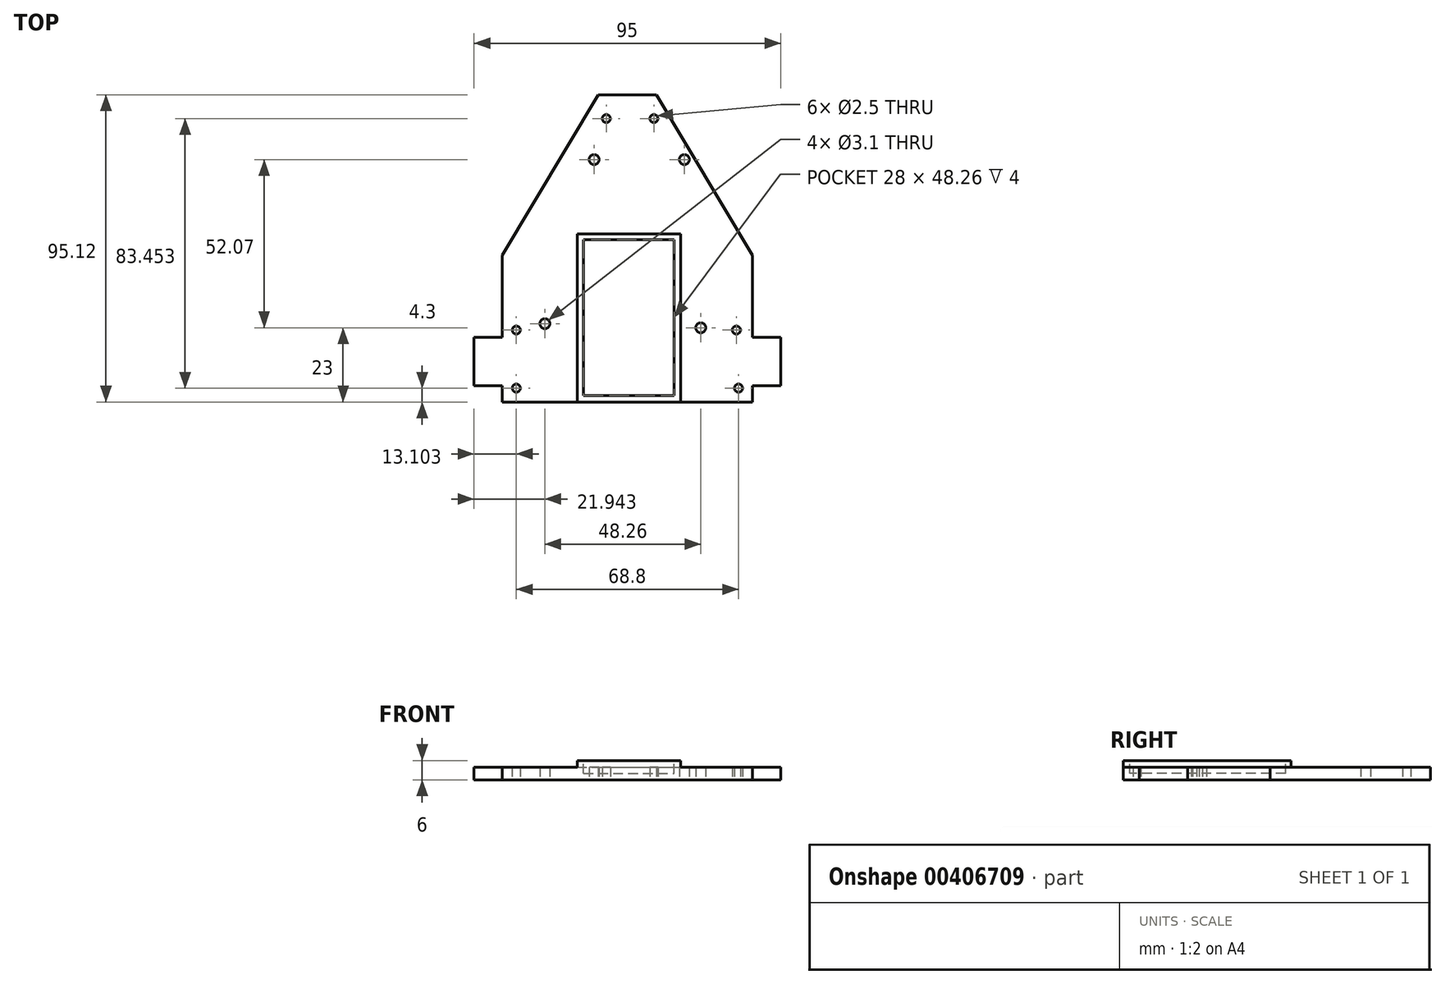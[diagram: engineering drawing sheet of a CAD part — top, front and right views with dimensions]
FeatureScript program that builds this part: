
annotation { "Feature Type Name" : "Feature", "Feature Type Description" : "" }
export const myFeature = defineFeature(function(context is Context, id is Id, definition is map)
    precondition{}
    {
        {
            var Q0;
            Q0=qCreatedBy(makeId("Top.planeOp"),FACE);
            var sketch = newSketch(context, id + "F0", { "sketchPlane" : qUnion([Q0])});
            skLineSegment(sketch, "E0", {"start": v(-31.63, 74.2) * mm, "end": v(-13.63, 74.2) * mm});
            skLineSegment(sketch, "E1", {"start": v(-13.63, 74.2) * mm, "end": v(16.07, 24.57) * mm});
            skLineSegment(sketch, "E2", {"start": v(16.07, 24.57) * mm, "end": v(16.07, -0.93) * mm});
            skLineSegment(sketch, "E3", {"start": v(16.07, -0.93) * mm, "end": v(24.87, -0.93) * mm});
            skLineSegment(sketch, "E4", {"start": v(24.87, -0.93) * mm, "end": v(24.87, -15.93) * mm});
            skLineSegment(sketch, "E5", {"start": v(24.87, -15.93) * mm, "end": v(16.07, -15.93) * mm});
            skLineSegment(sketch, "E6", {"start": v(16.07, -15.93) * mm, "end": v(16.07, -20.93) * mm});
            skLineSegment(sketch, "E7", {"start": v(16.07, -20.93) * mm, "end": v(-61.33, -20.93) * mm});
            skLineSegment(sketch, "E8", {"start": v(-61.33, -20.93) * mm, "end": v(-61.33, -15.93) * mm});
            skLineSegment(sketch, "E9", {"start": v(-61.33, -15.93) * mm, "end": v(-70.13, -15.93) * mm});
            skLineSegment(sketch, "E10", {"start": v(-70.13, -15.93) * mm, "end": v(-70.13, -0.93) * mm});
            skLineSegment(sketch, "E11", {"start": v(-70.13, -0.93) * mm, "end": v(-61.33, -0.93) * mm});
            skLineSegment(sketch, "E12", {"start": v(-61.33, -0.93) * mm, "end": v(-61.33, 24.57) * mm});
            skLineSegment(sketch, "E13", {"start": v(-61.33, 24.57) * mm, "end": v(-31.63, 74.2) * mm});
            skCircle(sketch, "E14", {"center": v(-29.16, 66.82) * mm, "radius": 1.25 * mm});
            skCircle(sketch, "E15", {"center": v(-14.42, 66.82) * mm, "radius": 1.25 * mm});
            skCircle(sketch, "E16", {"center": v(-57.03, 1.37) * mm, "radius": 1.25 * mm});
            skCircle(sketch, "E17", {"center": v(-57.03, -16.63) * mm, "radius": 1.25 * mm});
            skCircle(sketch, "E18", {"center": v(11.12, 1.37) * mm, "radius": 1.25 * mm});
            skCircle(sketch, "E19", {"center": v(11.77, -16.63) * mm, "radius": 1.25 * mm});
            skCircle(sketch, "E20", {"center": v(-48.19, 3.34) * mm, "radius": 1.55 * mm});
            skCircle(sketch, "E21", {"center": v(0.07, 2.07) * mm, "radius": 1.55 * mm});
            skCircle(sketch, "E22", {"center": v(-32.95, 54.14) * mm, "radius": 1.55 * mm});
            skCircle(sketch, "E23", {"center": v(-5, 54.14) * mm, "radius": 1.55 * mm});
            skSolve(sketch);
        }
        {
            var Q0;
            Q0 = qSketchRegion(id + "F0", true);
            extrude(context, id + "F1", {"entities" : qUnion([Q0]), "depth" : 4 * mm});
        }
        {
            var Q0;
            Q0=makeQuery(id+"F1.opExtrude","SWEPT_BODY",BODY,{"disambiguationData":[OSD([sQuery(id+"F0.wireOp",EDGE,"E0"),sQuery(id+"F0.wireOp",EDGE,"E1"),sQuery(id+"F0.wireOp",EDGE,"E2"),sQuery(id+"F0.wireOp",EDGE,"E3"),sQuery(id+"F0.wireOp",EDGE,"E4"),sQuery(id+"F0.wireOp",EDGE,"E5"),sQuery(id+"F0.wireOp",EDGE,"E6"),sQuery(id+"F0.wireOp",EDGE,"E7"),sQuery(id+"F0.wireOp",EDGE,"E8"),sQuery(id+"F0.wireOp",EDGE,"E9"),sQuery(id+"F0.wireOp",EDGE,"E10"),sQuery(id+"F0.wireOp",EDGE,"E11"),sQuery(id+"F0.wireOp",EDGE,"E12"),sQuery(id+"F0.wireOp",EDGE,"E13"),sQuery(id+"F0.wireOp",EDGE,"E14"),sQuery(id+"F0.wireOp",EDGE,"E15"),sQuery(id+"F0.wireOp",EDGE,"E16"),sQuery(id+"F0.wireOp",EDGE,"E17"),sQuery(id+"F0.wireOp",EDGE,"E18"),sQuery(id+"F0.wireOp",EDGE,"E19"),sQuery(id+"F0.wireOp",EDGE,"E20"),sQuery(id+"F0.wireOp",EDGE,"E21"),sQuery(id+"F0.wireOp",EDGE,"E22"),sQuery(id+"F0.wireOp",EDGE,"E23")])]});
            transform(context, id + "F2", {"entities" : qUnion([Q0]), "transformType" : TransformType.TRANSLATION_3D, "dx" : 0 * mm, "dy" : 0 * mm, "dz" : 7 * mm, "makeCopy" : true});
        }
        {
            var Q0;
            Q0=makeQuery(id+"F2.opPattern","COPY",BODY,{"derivedFrom":makeQuery(id+"F1.opExtrude","SWEPT_BODY",BODY,{"disambiguationData":[OSD([sQuery(id+"F0.wireOp",EDGE,"E0"),sQuery(id+"F0.wireOp",EDGE,"E1"),sQuery(id+"F0.wireOp",EDGE,"E2"),sQuery(id+"F0.wireOp",EDGE,"E3"),sQuery(id+"F0.wireOp",EDGE,"E4"),sQuery(id+"F0.wireOp",EDGE,"E5"),sQuery(id+"F0.wireOp",EDGE,"E6"),sQuery(id+"F0.wireOp",EDGE,"E7"),sQuery(id+"F0.wireOp",EDGE,"E8"),sQuery(id+"F0.wireOp",EDGE,"E9"),sQuery(id+"F0.wireOp",EDGE,"E10"),sQuery(id+"F0.wireOp",EDGE,"E11"),sQuery(id+"F0.wireOp",EDGE,"E12"),sQuery(id+"F0.wireOp",EDGE,"E13"),sQuery(id+"F0.wireOp",EDGE,"E14"),sQuery(id+"F0.wireOp",EDGE,"E15"),sQuery(id+"F0.wireOp",EDGE,"E16"),sQuery(id+"F0.wireOp",EDGE,"E17"),sQuery(id+"F0.wireOp",EDGE,"E18"),sQuery(id+"F0.wireOp",EDGE,"E19"),sQuery(id+"F0.wireOp",EDGE,"E20"),sQuery(id+"F0.wireOp",EDGE,"E21"),sQuery(id+"F0.wireOp",EDGE,"E22"),sQuery(id+"F0.wireOp",EDGE,"E23")])]}),"instanceName":"1"});
            deleteBodies(context, id + "F3", {"entities" : qUnion([Q0])});
        }
        {
            var Q0;
            Q0=makeQuery(id+"F1.opExtrude","SWEPT_BODY",BODY,{"disambiguationData":[OSD([sQuery(id+"F0.wireOp",EDGE,"E0"),sQuery(id+"F0.wireOp",EDGE,"E1"),sQuery(id+"F0.wireOp",EDGE,"E2"),sQuery(id+"F0.wireOp",EDGE,"E3"),sQuery(id+"F0.wireOp",EDGE,"E4"),sQuery(id+"F0.wireOp",EDGE,"E5"),sQuery(id+"F0.wireOp",EDGE,"E6"),sQuery(id+"F0.wireOp",EDGE,"E7"),sQuery(id+"F0.wireOp",EDGE,"E8"),sQuery(id+"F0.wireOp",EDGE,"E9"),sQuery(id+"F0.wireOp",EDGE,"E10"),sQuery(id+"F0.wireOp",EDGE,"E11"),sQuery(id+"F0.wireOp",EDGE,"E12"),sQuery(id+"F0.wireOp",EDGE,"E13"),sQuery(id+"F0.wireOp",EDGE,"E14"),sQuery(id+"F0.wireOp",EDGE,"E15"),sQuery(id+"F0.wireOp",EDGE,"E16"),sQuery(id+"F0.wireOp",EDGE,"E17"),sQuery(id+"F0.wireOp",EDGE,"E18"),sQuery(id+"F0.wireOp",EDGE,"E19"),sQuery(id+"F0.wireOp",EDGE,"E20"),sQuery(id+"F0.wireOp",EDGE,"E21"),sQuery(id+"F0.wireOp",EDGE,"E22"),sQuery(id+"F0.wireOp",EDGE,"E23")])]});
            transform(context, id + "F4", {"entities" : qUnion([Q0]), "transformType" : TransformType.TRANSLATION_3D, "dx" : 0 * mm, "dy" : 0 * mm, "dz" : 6 * mm, "makeCopy" : true});
        }
        {
            var Q0;
            Q0=makeQuery(id+"F4.opPattern","COPY",BODY,{"derivedFrom":makeQuery(id+"F1.opExtrude","SWEPT_BODY",BODY,{"disambiguationData":[OSD([sQuery(id+"F0.wireOp",EDGE,"E0"),sQuery(id+"F0.wireOp",EDGE,"E1"),sQuery(id+"F0.wireOp",EDGE,"E2"),sQuery(id+"F0.wireOp",EDGE,"E3"),sQuery(id+"F0.wireOp",EDGE,"E4"),sQuery(id+"F0.wireOp",EDGE,"E5"),sQuery(id+"F0.wireOp",EDGE,"E6"),sQuery(id+"F0.wireOp",EDGE,"E7"),sQuery(id+"F0.wireOp",EDGE,"E8"),sQuery(id+"F0.wireOp",EDGE,"E9"),sQuery(id+"F0.wireOp",EDGE,"E10"),sQuery(id+"F0.wireOp",EDGE,"E11"),sQuery(id+"F0.wireOp",EDGE,"E12"),sQuery(id+"F0.wireOp",EDGE,"E13"),sQuery(id+"F0.wireOp",EDGE,"E14"),sQuery(id+"F0.wireOp",EDGE,"E15"),sQuery(id+"F0.wireOp",EDGE,"E16"),sQuery(id+"F0.wireOp",EDGE,"E17"),sQuery(id+"F0.wireOp",EDGE,"E18"),sQuery(id+"F0.wireOp",EDGE,"E19"),sQuery(id+"F0.wireOp",EDGE,"E20"),sQuery(id+"F0.wireOp",EDGE,"E21"),sQuery(id+"F0.wireOp",EDGE,"E22"),sQuery(id+"F0.wireOp",EDGE,"E23")])]}),"instanceName":"1"});
            deleteBodies(context, id + "F5", {"entities" : qUnion([Q0])});
        }
        {
            var Q0;
            Q0=makeQuery(id+"F1.opExtrude","CAP_FACE",FACE,{"disambiguationData":[OSD([sQuery(id+"F0.wireOp",EDGE,"E0"),sQuery(id+"F0.wireOp",EDGE,"E1"),sQuery(id+"F0.wireOp",EDGE,"E2"),sQuery(id+"F0.wireOp",EDGE,"E3"),sQuery(id+"F0.wireOp",EDGE,"E4"),sQuery(id+"F0.wireOp",EDGE,"E5"),sQuery(id+"F0.wireOp",EDGE,"E6"),sQuery(id+"F0.wireOp",EDGE,"E7"),sQuery(id+"F0.wireOp",EDGE,"E8"),sQuery(id+"F0.wireOp",EDGE,"E9"),sQuery(id+"F0.wireOp",EDGE,"E10"),sQuery(id+"F0.wireOp",EDGE,"E11"),sQuery(id+"F0.wireOp",EDGE,"E12"),sQuery(id+"F0.wireOp",EDGE,"E13"),sQuery(id+"F0.wireOp",EDGE,"E14"),sQuery(id+"F0.wireOp",EDGE,"E15"),sQuery(id+"F0.wireOp",EDGE,"E16"),sQuery(id+"F0.wireOp",EDGE,"E17"),sQuery(id+"F0.wireOp",EDGE,"E18"),sQuery(id+"F0.wireOp",EDGE,"E19"),sQuery(id+"F0.wireOp",EDGE,"E20"),sQuery(id+"F0.wireOp",EDGE,"E21"),sQuery(id+"F0.wireOp",EDGE,"E22"),sQuery(id+"F0.wireOp",EDGE,"E23")])],"isStart":false});
            var sketch = newSketch(context, id + "F6", { "sketchPlane" : qUnion([Q0])});
            skLineSegment(sketch, "E24.bottom", {"start": v(-38.19, -20.93) * mm, "end": v(-6.19, -20.93) * mm});
            skLineSegment(sketch, "E24.top", {"start": v(-38.19, 31.07) * mm, "end": v(-6.19, 31.07) * mm});
            skLineSegment(sketch, "E24.left", {"start": v(-38.19, -20.93) * mm, "end": v(-38.19, 31.07) * mm});
            skLineSegment(sketch, "E24.right", {"start": v(-6.19, -20.93) * mm, "end": v(-6.19, 31.07) * mm});
            skSolve(sketch);
        }
        {
            var Q0;
            Q0 = qSketchRegion(id + "F6", true);
            extrude(context, id + "F7", {"entities" : qUnion([Q0]), "operationType" : NewBodyOperationType.ADD, "depth" : 2 * mm});
        }
        {
            var Q0;
            Q0=makeQuery(id+"F7.opExtrude","CAP_FACE",FACE,{"disambiguationData":[OSD([sQuery(id+"F6.wireOp",EDGE,"E24.bottom"),sQuery(id+"F6.wireOp",EDGE,"E24.top"),sQuery(id+"F6.wireOp",EDGE,"E24.left"),sQuery(id+"F6.wireOp",EDGE,"E24.right")])],"isStart":false});
            var sketch = newSketch(context, id + "F8", { "sketchPlane" : qUnion([Q0])});
            skLineSegment(sketch, "E25.bottom", {"start": v(-36.19, 29.33) * mm, "end": v(-8.19, 29.33) * mm});
            skLineSegment(sketch, "E25.top", {"start": v(-36.19, -18.93) * mm, "end": v(-8.19, -18.93) * mm});
            skLineSegment(sketch, "E25.left", {"start": v(-36.19, 29.33) * mm, "end": v(-36.19, -18.93) * mm});
            skLineSegment(sketch, "E25.right", {"start": v(-8.19, 29.33) * mm, "end": v(-8.19, -18.93) * mm});
            skSolve(sketch);
        }
        {
            var Q0;
            Q0 = qSketchRegion(id + "F8", true);
            extrude(context, id + "F9", {"entities" : qUnion([Q0]), "operationType" : NewBodyOperationType.REMOVE, "oppositeDirection" : true, "depth" : 4 * mm});
        }
    });
